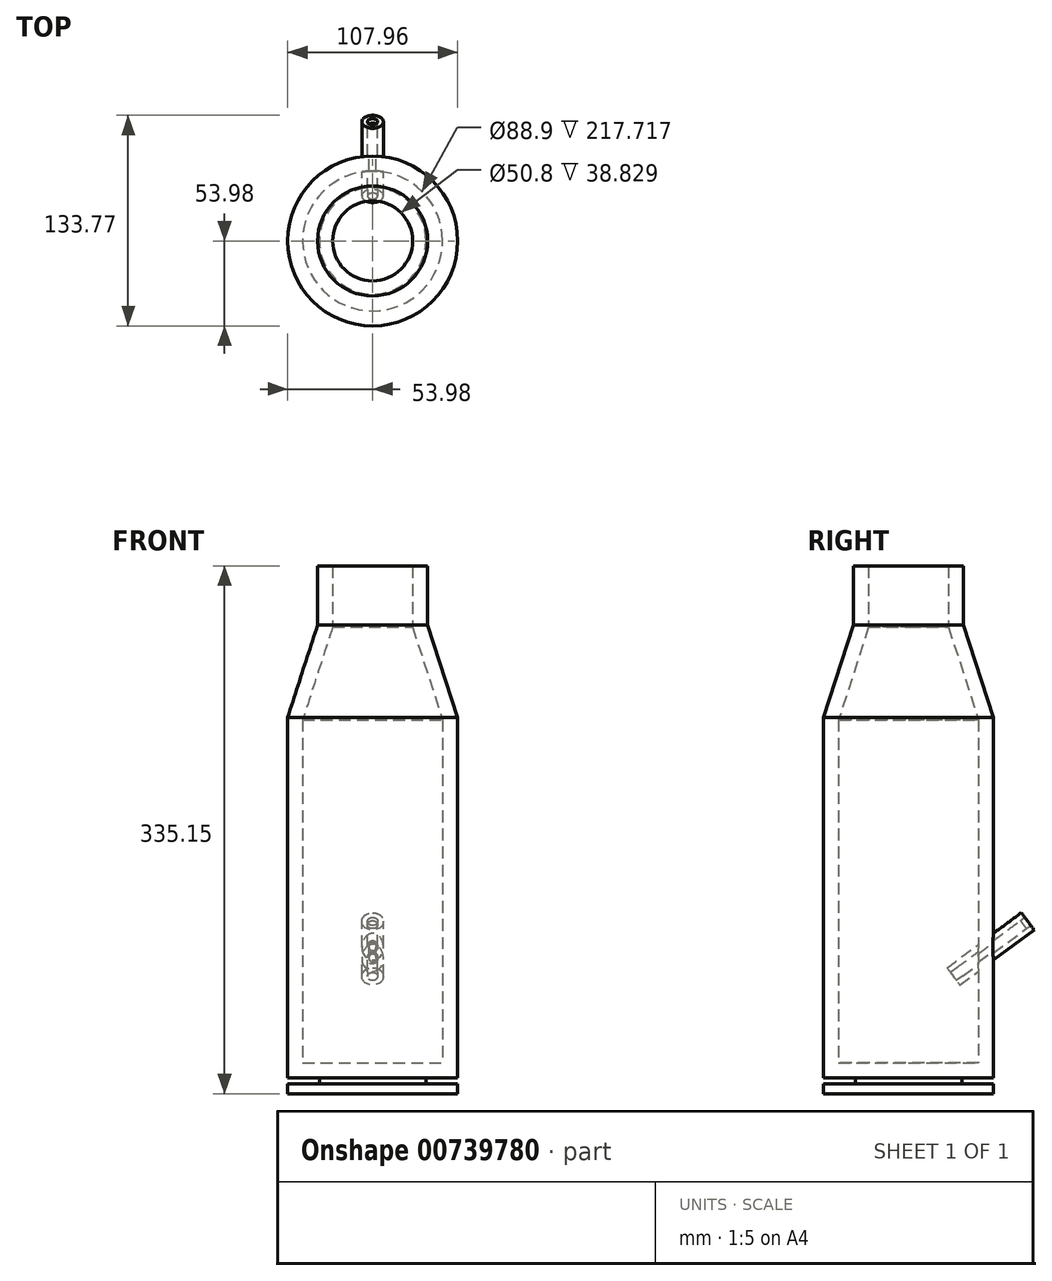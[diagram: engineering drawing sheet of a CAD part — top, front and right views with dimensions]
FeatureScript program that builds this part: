
annotation { "Feature Type Name" : "Feature", "Feature Type Description" : "" }
export const myFeature = defineFeature(function(context is Context, id is Id, definition is map)
    precondition{}
    {
        {
            var Q0;
            Q0=qCreatedBy(makeId("Right.planeOp"),FACE);
            var sketch = newSketch(context, id + "F0", { "sketchPlane" : qUnion([Q0])});
            skLineSegment(sketch, "E0", {"start": v(0, -185.06) * mm, "end": v(53.98, -185.06) * mm});
            skLineSegment(sketch, "E1", {"start": v(53.98, -185.06) * mm, "end": v(53.98, -178.7) * mm});
            skLineSegment(sketch, "E2", {"start": v(53.98, -178.7) * mm, "end": v(33.86, -178.7) * mm});
            skLineSegment(sketch, "E3", {"start": v(33.86, -178.7) * mm, "end": v(33.86, -174.9) * mm});
            skLineSegment(sketch, "E4", {"start": v(33.86, -174.9) * mm, "end": v(53.98, -174.9) * mm});
            skLineSegment(sketch, "E5", {"start": v(53.98, -174.9) * mm, "end": v(53.98, 53.85) * mm});
            skLineSegment(sketch, "E6", {"start": v(53.98, 53.85) * mm, "end": v(34.92, 112.76) * mm});
            skLineSegment(sketch, "E7", {"start": v(34.92, 112.76) * mm, "end": v(34.92, 150.1) * mm});
            skLineSegment(sketch, "E8.0", {"start": v(25.4, 111.26) * mm, "end": v(25.4, 150.1) * mm});
            skLineSegment(sketch, "E8.1", {"start": v(44.45, 52.35) * mm, "end": v(25.4, 111.26) * mm});
            skLineSegment(sketch, "E8.2", {"start": v(44.45, -165.37) * mm, "end": v(44.45, 52.35) * mm});
            skLineSegment(sketch, "E9", {"start": v(25.4, 150.1) * mm, "end": v(34.92, 150.1) * mm});
            skLineSegment(sketch, "E10", {"start": v(44.45, -165.37) * mm, "end": v(33.86, -174.9) * mm});
            skLineSegment(sketch, "E11", {"start": v(33.86, -174.9) * mm, "end": v(0, -174.9) * mm});
            skLineSegment(sketch, "E12", {"start": v(0, -174.9) * mm, "end": v(0, -185.06) * mm});
            skLineSegment(sketch, "E13", {"start": v(44.45, -165.37) * mm, "end": v(0, -165.37) * mm});
            skLineSegment(sketch, "E14", {"start": v(0, -165.37) * mm, "end": v(0, -174.9) * mm});
            skLineSegment(sketch, "E15", {"start": v(0, -165.37) * mm, "end": v(0, 183.27) * mm, "construction": true});
            skSolve(sketch);
        }
        {
            var Q0;
            Q0 = qSketchRegion(id + "F0", true);
            var Q1;
            Q1=sQuery(id+"F0.wireOp",EDGE,"E15");
            revolve(context, id + "F1", {"surfaceOperationType" : NewSurfaceOperationType.NEW, "entities" : qUnion([Q0]), "axis" : qUnion([Q1]), "revolveType" : RevolveType.FULL});
        }
        {
            var Q0;
            Q0=qCreatedBy(makeId("Right.planeOp"),FACE);
            var sketch = newSketch(context, id + "F2", { "sketchPlane" : qUnion([Q0])});
            skLineSegment(sketch, "E16", {"start": v(24.46, -105.07) * mm, "end": v(71.64, -70.13) * mm});
            skLineSegment(sketch, "E17", {"start": v(71.06, -75.13) * mm, "end": v(30.63, -105.07) * mm});
            skLineSegment(sketch, "E18", {"start": v(24.46, -105.07) * mm, "end": v(26.64, -108) * mm});
            skLineSegment(sketch, "E19", {"start": v(26.64, -108) * mm, "end": v(30.63, -105.07) * mm});
            skLineSegment(sketch, "E20", {"start": v(71.64, -70.13) * mm, "end": v(73.8, -73.05) * mm});
            skLineSegment(sketch, "E21", {"start": v(73.8, -73.05) * mm, "end": v(71.06, -75.13) * mm});
            skLineSegment(sketch, "E22", {"start": v(76.4, -75.13) * mm, "end": v(28.42, -110.65) * mm, "construction": true});
            skSolve(sketch);
        }
        {
            var Q0;
            Q0 = qSketchRegion(id + "F2", true);
            var Q1;
            Q1=sQuery(id+"F2.wireOp",EDGE,"E22");
            revolve(context, id + "F3", {"operationType" : NewBodyOperationType.ADD, "surfaceOperationType" : NewSurfaceOperationType.NEW, "entities" : qUnion([Q0]), "axis" : qUnion([Q1]), "revolveType" : RevolveType.FULL});
        }
        {
            var Q0;
            Q0=makeQuery(id+"F3.opRevolve","SWEPT_FACE",FACE,{"disambiguationData":[OSD([sQuery(id+"F2.wireOp",EDGE,"E20")])]});
            var sketch = newSketch(context, id + "F4", { "sketchPlane" : qUnion([Q0])});
            skCircle(sketch, "E23", {"center": v(0, -105.84) * mm, "radius": 2.15 * mm});
            skSolve(sketch);
        }
        {
            var Q0;
            Q0 = qSketchRegion(id + "F4", true);
            extrude(context, id + "F5", {"entities" : qUnion([Q0]), "operationType" : NewBodyOperationType.REMOVE, "oppositeDirection" : true, "depth" : 50.8 * mm, "offsetDistance" : 25.4 * mm});
        }
    });
